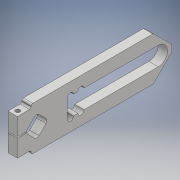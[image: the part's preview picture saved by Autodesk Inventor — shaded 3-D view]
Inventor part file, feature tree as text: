
AUTODESK INVENTOR PART (.ipt)
format: ipt  version: 2017 (Build 210142000, 142)  size: 190,464 bytes
history: native  units: mm
features: sketch x3, extrude x2, hole x1
ambient origin geometry x8: Origin, YZ Plane, XZ Plane, XY Plane, X Axis, Y Axis, Z Axis, Center Point
bodies: Solide1 (feature_tree)
feature tree (6):
  extrude  "Extrusion1"  Depth=70.0mm
  extrude  "Extrusion2"  Depth=10.0mm
  hole  "Perçage1"  [1 undecoded]
  sketch  "Esquisse1"
  sketch  "Esquisse2"
  sketch  "Esquisse3"
note: 1 required parameter value undecoded (feature->parameter linkage not recoverable at this tier; creation-order binding heuristic only, values carry confidence <= 0.55)
